SOLIDWORKS PART (.sldprt)
format: sldprt  version: not decoded by parser v0  size: 138,240 bytes
history: native  units: mm
features: sketch x2, fillet x2, chamfer x2, material x1, extrude x1, cut_extrude x1 (+16 scaffold rows collapsed)
feature tree (25):
  scaffold x16  (default folders/planes/origin — collapsed)
  material  "Plain Carbon Steel"
  sketch  "Sketch1"
  extrude  "Boss-Extrude1"  Depth=4.7625mm
  sketch  "Sketch2"  dims[D1=3.5mm]
  cut_extrude  "Cut-Extrude1"  [1 undecoded]
  fillet  "Fillet1"  Radius=10mm
  chamfer  "Chamfer1"  Distance=2mm Angle=45deg
  chamfer  "Chamfer2"  Distance=1mm Angle=45deg
  fillet  "Fillet2"  Radius=3mm
decode coverage: 6 of 8 modeling features carry decoded parameters
note: 1 parameter value undecoded
note: suppression state not decoded; provenance and decode notes live in map.json
